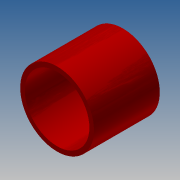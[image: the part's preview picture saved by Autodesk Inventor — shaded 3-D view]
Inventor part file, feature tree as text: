
AUTODESK INVENTOR PART (.ipt)
format: ipt  version: 2017.3 (Build 213257000, 257)  size: 106,496 bytes
history: native  units: in
note: dims shown in document units (in); Inventor stores cm internally (conversion verified against a paired STEP export)
features: other x3, extrude x2, sketch x2
ambient origin geometry x8: Origin, YZ Plane, XZ Plane, XY Plane, X Axis, Y Axis, Z Axis, Center Point
bodies: Solid1 (feature_tree)
feature tree (7):
  other  "A1-19027-400-09 HCWI liner - drain.ipt"
  extrude  "Extrusion1"  Depth=0.5in TaperAngle=0.0deg
  extrude  "Extrusion2"  [1 undecoded]
  other  "Solid1::A1-19027-400-09 HCWI liner - drain.ipt"
  other  "TaggingFeature1"
  sketch  "Sketch2"  dims[d0=0.3937in d1=0.5in d2=0.5in d3=0.0in d4=0.0in]
  sketch  "Sketch3"  dims[d5=0.5in d6=1.0in d7=0.0in d8=0.0in]
note: 1 required parameter value undecoded (feature->parameter linkage not recoverable at this tier; creation-order binding heuristic only, values carry confidence <= 0.55)
